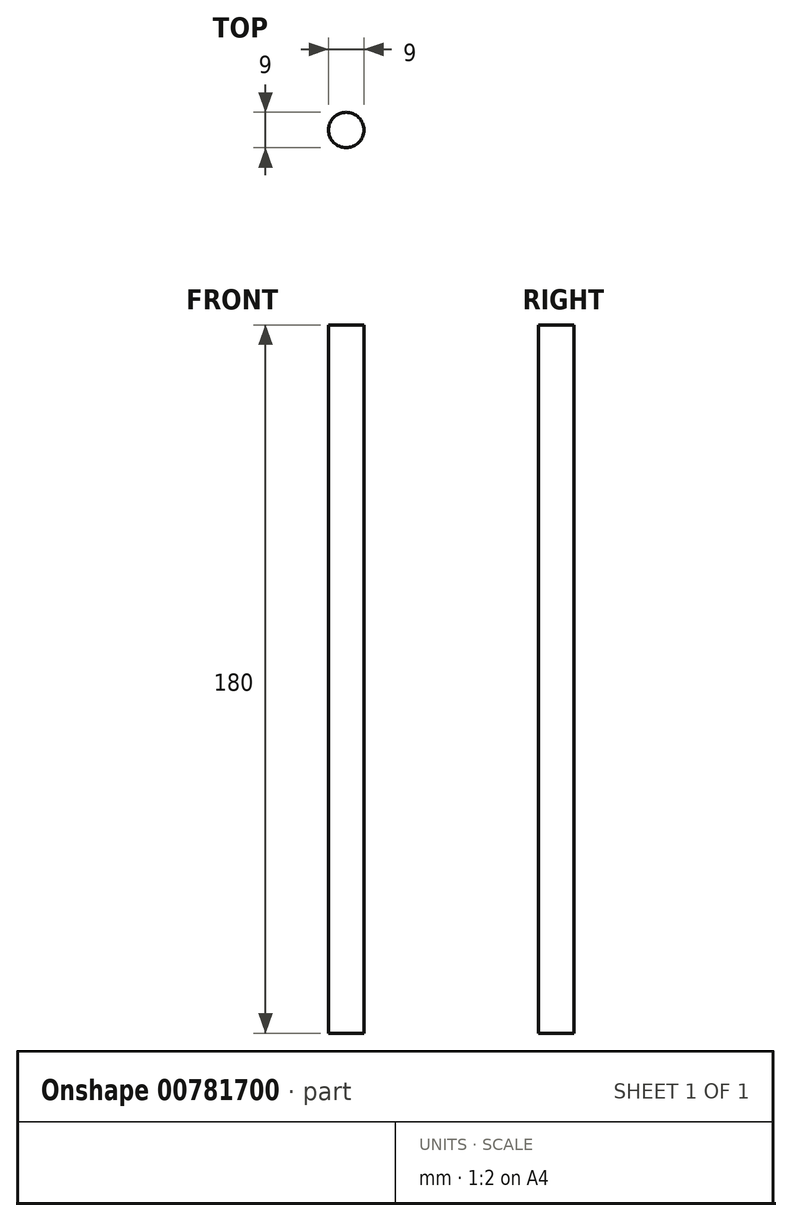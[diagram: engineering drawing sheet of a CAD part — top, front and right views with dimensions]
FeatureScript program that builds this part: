
annotation { "Feature Type Name" : "Feature", "Feature Type Description" : "" }
export const myFeature = defineFeature(function(context is Context, id is Id, definition is map)
    precondition{}
    {
        {
            var Q0;
            Q0=qCreatedBy(makeId("Top.planeOp"),FACE);
            var sketch = newSketch(context, id + "F0", { "sketchPlane" : qUnion([Q0])});
            skCircle(sketch, "E0", {"center": v(0.74, 0) * mm, "radius": 4.5 * mm});
            skSolve(sketch);
        }
        {
            var Q0;
            Q0 = qSketchRegion(id + "F0", true);
            extrude(context, id + "F1", {"entities" : qUnion([Q0]), "depth" : 180 * mm, "offsetDistance" : 25 * mm});
        }
    });
